# Revit family: BE_99814_de_DE
name_source: partatom
category: Leuchten
units: mm (PartAtom-declared; Revit-internal decimal feet)

## family parameters
Basisbauteil = Fläche
Beim Laden mit Abzugskörper schneiden = Ja
Bemaßung runder Anschluss = Durchmesser verwenden
Gemeinsam genutzt = Nein
Lichtquelle = Ja
Raumberechnungspunkt = Ja
Teiletyp = Normal

## types (1)
- BEGA_99814_K3
    AC/DC = DC
    Aktualisierung = 2022-05-20T04:00:08
    Anschlussleitung = 3.0 m 05RN8-F 2 × 1²
    BEGA_Dummy = Nein
    BEGA_IES = Ja
    BEGA_Intern = Ja
    BEGA_Intern_Konstruktion = Ja
    BEGA_Intern_an = Ja
    BEGA_Intern_aus = Ja
    Beschreibung = Schwimmbadleuchte
    Beschreibung_Sonderanfertigung = Hier können Sie Informationen zur Sonderanfertigung eintragen.
    Bestellnummer = 99814K3
    CE_Konformität = ja
    Datei für fotometrisches Netz = BE_99814K3.IES
    ENEC = ja
    Einbauöffnung = 210 mm
    Energieeffizienzklasse = LED A++ - A
    Farbfilter = 16777215
    Farbtemperatur = 3000 K
    Farbtemperaturverschiebung bei Dämpfen der Lampe = <Keine Auswahl>
    Farbwiedergabeindex = CRI > 80
    Gewicht = 3.2 kg
    Hersteller = BEGA
    LED_Modulbezeichnung = LED-1196/830
    Lampe = LED 15.5 W
    Lampenlichtstrom = 3010 lm
    Lastklassifizierung = Beleuchtung
    Lebensdauerkriterien = L70B50 @ 25 °C = 200000 h
    Leuchtenlichtstrom = 2257 lm
    Logo = BEGA_Logo.png
    M_A = Nein
    M_G = Nein
    M_W = Nein
    Material_02 = BEGA_Oberfläche_Silber_matt
    Material_03 = BEGA_Oberfläche_Weiss_matt
    Material_06 = BEGA_Oberfläche_Edelstahl_gebürstet
    Material_09 = BEGA_Glas_klar
    Material_11 = BEGA_Glas_opal
    Material_15 = BEGA_Leuchtmedium_matt
    Material_17 = BEGA_Reflektor
    Material_18 = BEGA_Gummi_schwarz
    Modell = 99814K3
    Neigungswinkel = 0.00°
    Netzteil_DALI_steuerbar = Nein
    Netzteil_dimmbar_1_bis_10V = Nein
    Produktdatenblatt = https://cdn.bega.com
    Scheinlast = 0 VA
    Schutzart = IP 68...10m
    Schutzklasse = III
    Sonderanfertigung = Nein
    Spannung = 24 V
    Typenbild = 99814.png
    URL = https://www.bega.com
    Umgebungstemperatur = 25 °C
    Vorgabe-Ansicht = 0 mm  [stored 0 ft]

note: [stored X ft] marks values corroborated as IEEE doubles in the binary element streams (Revit-internal decimal feet)
